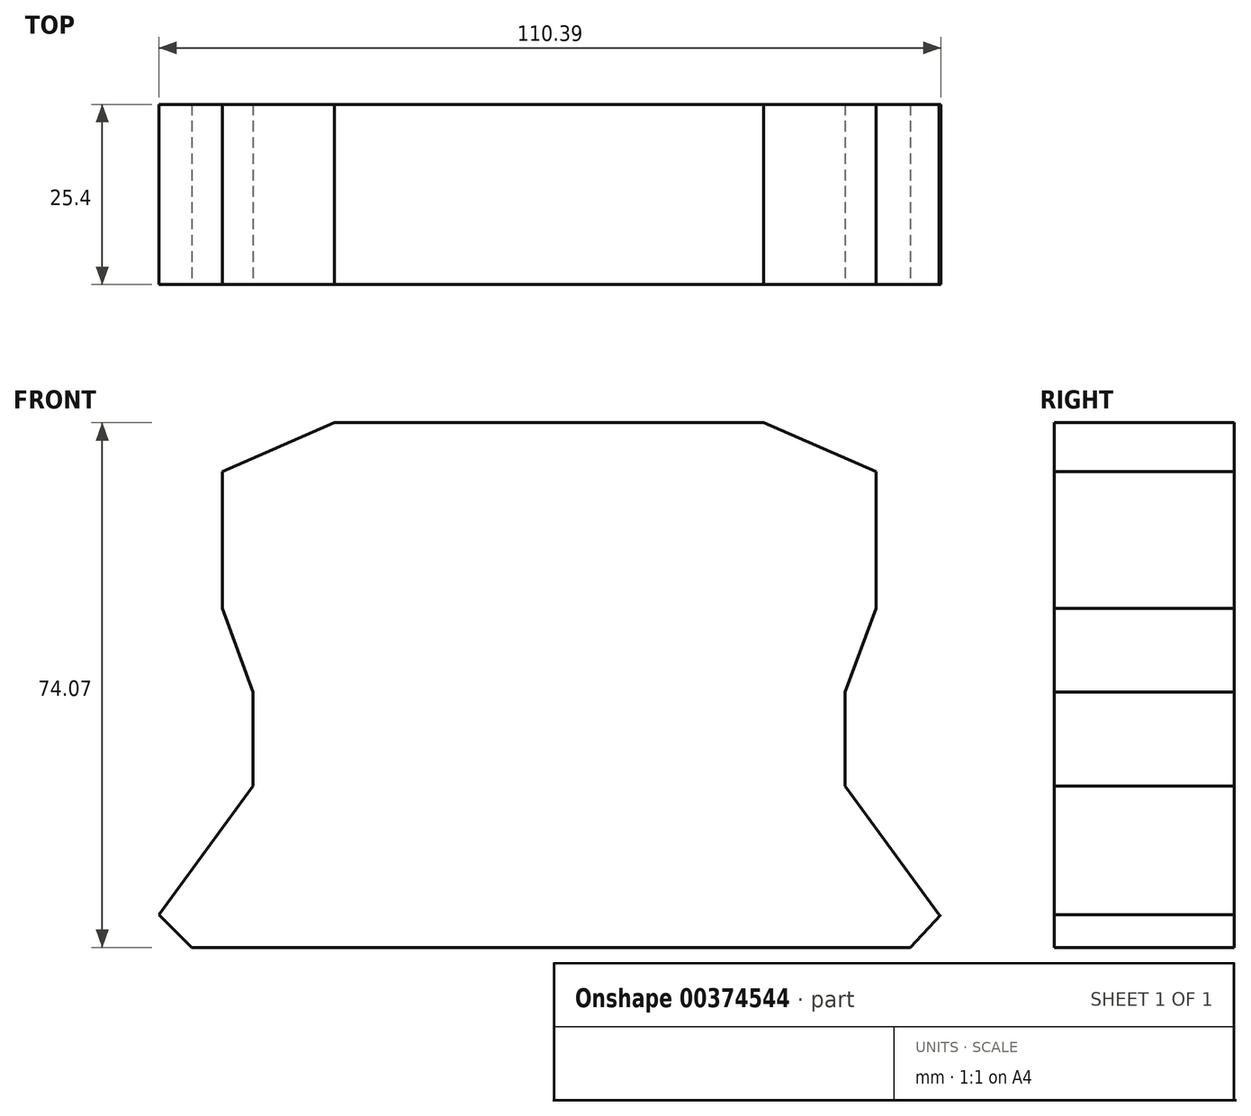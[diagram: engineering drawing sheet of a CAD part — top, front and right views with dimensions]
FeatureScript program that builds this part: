
annotation { "Feature Type Name" : "Feature", "Feature Type Description" : "" }
export const myFeature = defineFeature(function(context is Context, id is Id, definition is map)
    precondition{}
    {
        {
            var Q0;
            Q0=qCreatedBy(makeId("Front.planeOp"),FACE);
            var sketch = newSketch(context, id + "F0", { "sketchPlane" : qUnion([Q0])});
            skLineSegment(sketch, "E0", {"start": v(-50.45, -44.06) * mm, "end": v(51, -44.06) * mm});
            skLineSegment(sketch, "E1", {"start": v(51, -44.06) * mm, "end": v(55.33, -39.45) * mm});
            skLineSegment(sketch, "E2", {"start": v(-55.06, -39.45) * mm, "end": v(-50.45, -44.06) * mm});
            skLineSegment(sketch, "E3", {"start": v(-55.06, -39.45) * mm, "end": v(-41.8, -21.3) * mm});
            skLineSegment(sketch, "E4", {"start": v(-41.8, -21.3) * mm, "end": v(-41.8, -8.03) * mm});
            skLineSegment(sketch, "E5", {"start": v(-41.8, -8.03) * mm, "end": v(-46.13, 3.78) * mm});
            skLineSegment(sketch, "E6", {"start": v(-46.13, 3.78) * mm, "end": v(-46.13, 23.1) * mm});
            skLineSegment(sketch, "E7", {"start": v(-46.13, 23.1) * mm, "end": v(-30.27, 30.01) * mm});
            skLineSegment(sketch, "E8", {"start": v(-30.27, 30.01) * mm, "end": v(0, 30.01) * mm});
            skLineSegment(sketch, "E9.MirrorCS", {"start": v(30.27, 30.01) * mm, "end": v(0, 30.01) * mm});
            skLineSegment(sketch, "E10.MirrorCS", {"start": v(46.13, 23.1) * mm, "end": v(30.27, 30.01) * mm});
            skLineSegment(sketch, "E11.MirrorCS", {"start": v(46.13, 3.78) * mm, "end": v(46.13, 23.1) * mm});
            skLineSegment(sketch, "E12.MirrorCS", {"start": v(41.8, -8.03) * mm, "end": v(46.13, 3.78) * mm});
            skLineSegment(sketch, "E13.MirrorCS", {"start": v(41.8, -21.3) * mm, "end": v(41.8, -8.03) * mm});
            skLineSegment(sketch, "E14.MirrorCS", {"start": v(55.06, -39.45) * mm, "end": v(41.8, -21.3) * mm});
            skSolve(sketch);
        }
        {
            var Q0;
            Q0 = qSketchRegion(id + "F0", true);
            var Q1;
            Q1=sQuery(id+"F0.wireOp",EDGE,"E6");
            var Q2;
            Q2=sQuery(id+"F0.wireOp",EDGE,"E7");
            var Q3;
            Q3=sQuery(id+"F0.wireOp",EDGE,"E8");
            var Q4;
            Q4=sQuery(id+"F0.wireOp",EDGE,"E0");
            var Q5;
            Q5=sQuery(id+"F0.wireOp",EDGE,"E2");
            var Q6;
            Q6=sQuery(id+"F0.wireOp",EDGE,"E3");
            var Q7;
            Q7=sQuery(id+"F0.wireOp",EDGE,"E4");
            var Q8;
            Q8=sQuery(id+"F0.wireOp",EDGE,"E5");
            var Q9;
            Q9=sQuery(id+"F0.wireOp",EDGE,"E9.MirrorCS");
            var Q10;
            Q10=sQuery(id+"F0.wireOp",EDGE,"E10.MirrorCS");
            var Q11;
            Q11=sQuery(id+"F0.wireOp",EDGE,"E11.MirrorCS");
            var Q12;
            Q12=sQuery(id+"F0.wireOp",EDGE,"E12.MirrorCS");
            var Q13;
            Q13=sQuery(id+"F0.wireOp",EDGE,"E13.MirrorCS");
            var Q14;
            Q14=sQuery(id+"F0.wireOp",EDGE,"E14.MirrorCS");
            var Q15;
            Q15=sQuery(id+"F0.wireOp",EDGE,"E1");
            extrude(context, id + "F1", {"entities" : qUnion([Q0]), "bodyType" : ToolBodyType.SURFACE, "surfaceEntities" : qUnion([Q1, Q2, Q3, Q4, Q5, Q6, Q7, Q8, Q9, Q10, Q11, Q12, Q13, Q14, Q15]), "depth" : 25.4 * mm});
        }
    });
